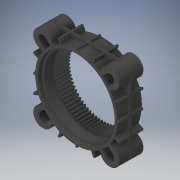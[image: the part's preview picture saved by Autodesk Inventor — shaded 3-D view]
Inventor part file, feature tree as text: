
AUTODESK INVENTOR PART (.ipt)
format: ipt  version: 2019 (Build 230136000, 136)  size: 1,947,648 bytes
history: native  units: in
note: dims shown in document units (in); Inventor stores cm internally (conversion verified against a paired STEP export)
features: fillet x1
ambient origin geometry x8: Origin, YZ Plane, XZ Plane, XY Plane, X Axis, Y Axis, Z Axis, Center Point
bodies: Solid1 (feature_tree)
feature tree (1):
  fillet  "Fillet12"  [1 undecoded]
note: 1 required parameter value undecoded (feature->parameter linkage not recoverable at this tier; creation-order binding heuristic only, values carry confidence <= 0.55)
